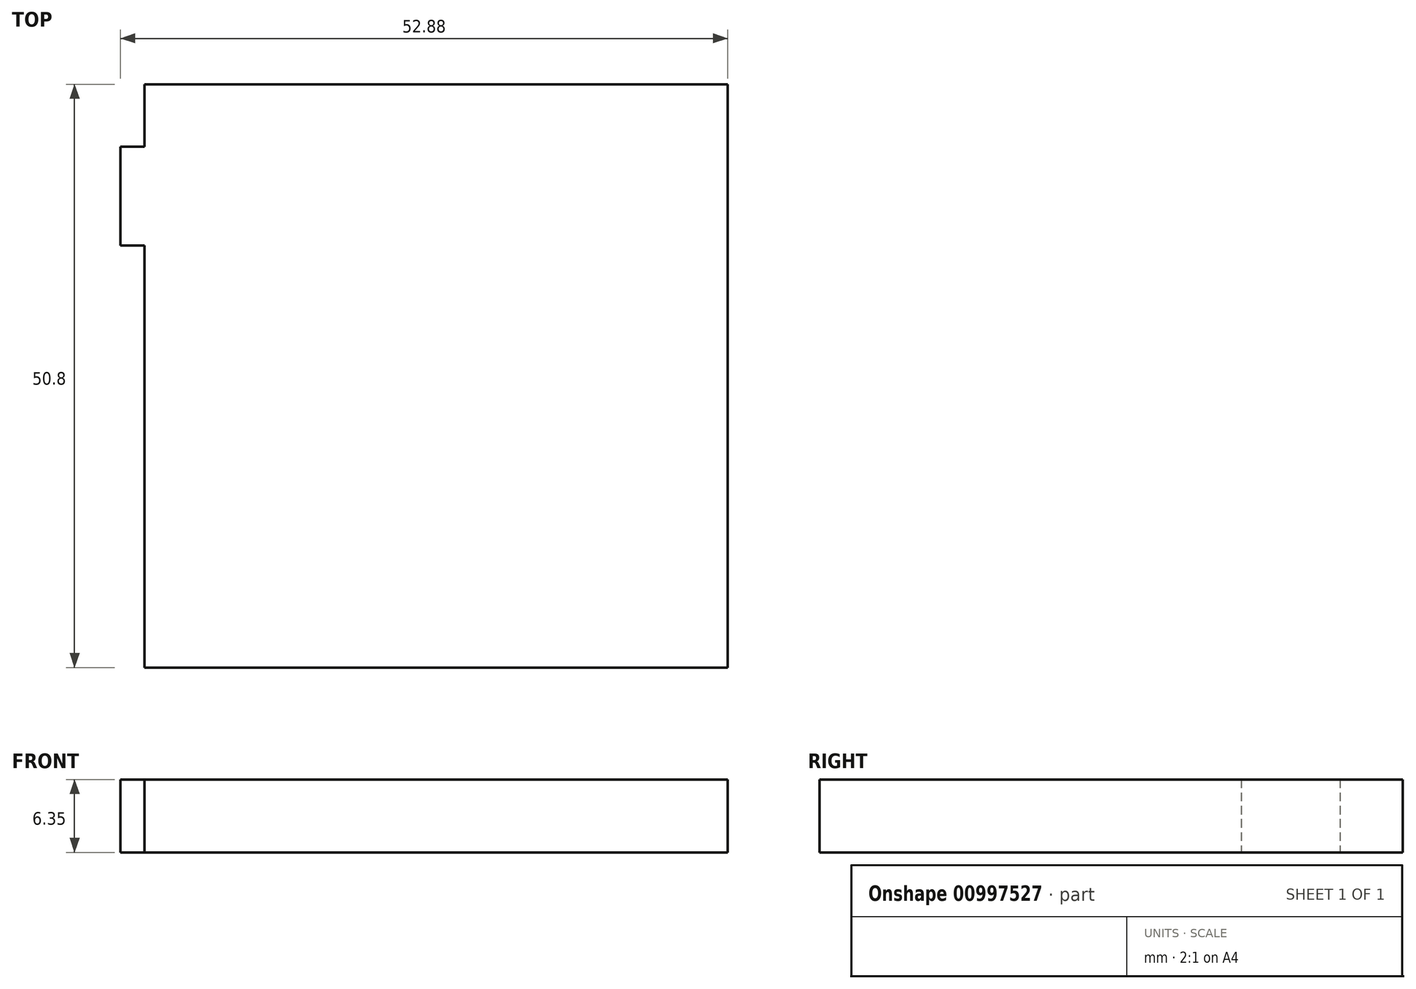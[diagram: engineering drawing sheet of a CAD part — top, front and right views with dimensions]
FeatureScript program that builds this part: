
annotation { "Feature Type Name" : "Feature", "Feature Type Description" : "" }
export const myFeature = defineFeature(function(context is Context, id is Id, definition is map)
    precondition{}
    {
        {
            var Q0;
            Q0=qCreatedBy(makeId("Top.planeOp"),FACE);
            var sketch = newSketch(context, id + "F0", { "sketchPlane" : qUnion([Q0])});
            skLineSegment(sketch, "E0.bottom", {"start": v(-25.4, -25.4) * mm, "end": v(25.4, -25.4) * mm});
            skLineSegment(sketch, "E0.top", {"start": v(-25.4, 25.4) * mm, "end": v(25.4, 25.4) * mm});
            skLineSegment(sketch, "E0.right", {"start": v(25.4, -25.4) * mm, "end": v(25.4, 25.4) * mm});
            skPoint(sketch, "E1", {"position": v(19.05, 19.05) * mm});
            skPoint(sketch, "E2", {"position": v(-19.05, -19.05) * mm});
            skLineSegment(sketch, "E3", {"start": v(-25.4, 25.4) * mm, "end": v(-25.4, 19.95) * mm});
            skLineSegment(sketch, "E4", {"start": v(-27.48, 19.95) * mm, "end": v(-25.4, 19.95) * mm});
            skLineSegment(sketch, "E5", {"start": v(-27.48, 19.95) * mm, "end": v(-27.48, 11.35) * mm});
            skLineSegment(sketch, "E6", {"start": v(-25.4, 11.35) * mm, "end": v(-27.48, 11.35) * mm});
            skLineSegment(sketch, "E7", {"start": v(-25.4, 11.35) * mm, "end": v(-25.4, -25.4) * mm});
            skSolve(sketch);
        }
        {
            var Q0;
            Q0=makeQuery(id+"F0.imprint","IMPRINT",FACE,{"disambiguationData":[TD([[makeQuery(id+"F0.imprint","IMPRINT",EDGE,{"derivedFrom":sQuery(id+"F0.wireOp",EDGE,"E0.bottom")}),1.0]])]});
            extrude(context, id + "F1", {"entities" : qUnion([Q0]), "depth" : 6.35 * mm, "offsetDistance" : 25.4 * mm});
        }
    });
